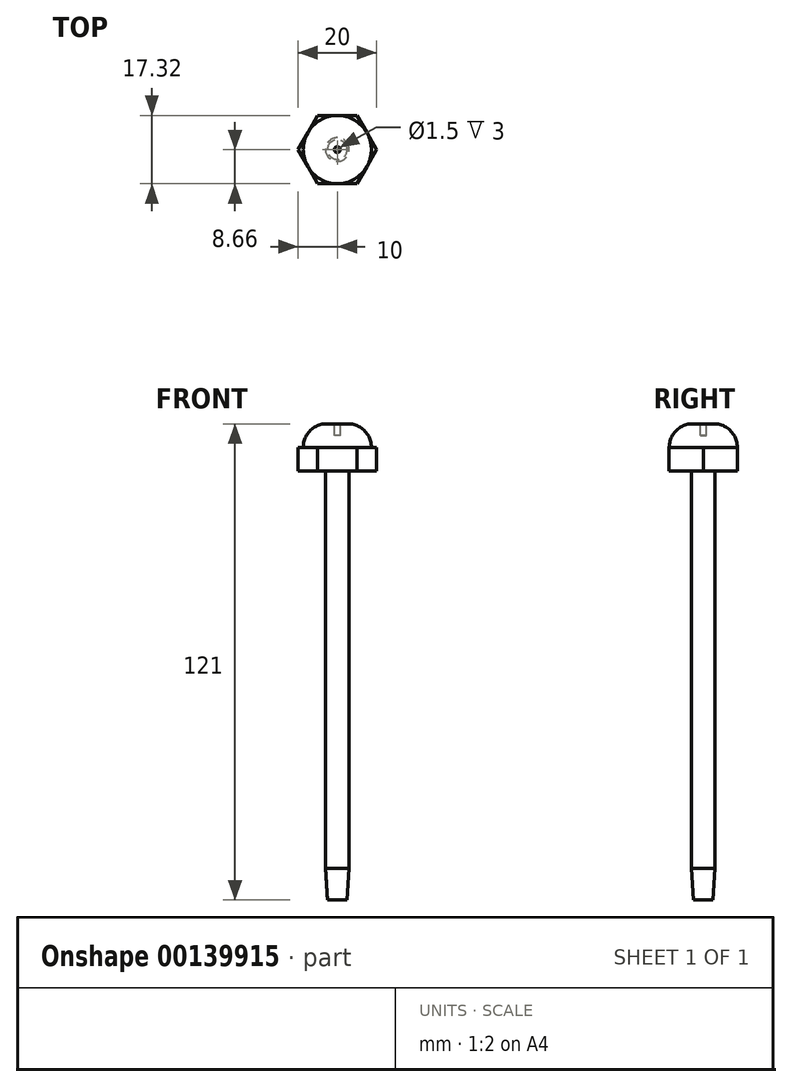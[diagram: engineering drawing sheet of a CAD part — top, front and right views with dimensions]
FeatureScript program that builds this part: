
annotation { "Feature Type Name" : "Feature", "Feature Type Description" : "" }
export const myFeature = defineFeature(function(context is Context, id is Id, definition is map)
    precondition{}
    {
        {
            var Q0;
            Q0=qCreatedBy(makeId("Top.planeOp"),FACE);
            var sketch = newSketch(context, id + "F0", { "sketchPlane" : qUnion([Q0])});
            skCircle(sketch, "E0", {"center": v(0, 0) * mm, "radius": 3 * mm});
            skLineSegment(sketch, "E1", {"start": v(-5, 8.66) * mm, "end": v(5, 8.66) * mm});
            skLineSegment(sketch, "E2", {"start": v(5, 8.66) * mm, "end": v(10, 0) * mm});
            skLineSegment(sketch, "E3", {"start": v(10, 0) * mm, "end": v(5, -8.66) * mm});
            skLineSegment(sketch, "E4", {"start": v(5, -8.66) * mm, "end": v(-5, -8.66) * mm});
            skLineSegment(sketch, "E5", {"start": v(-5, -8.66) * mm, "end": v(-10, 0) * mm});
            skLineSegment(sketch, "E6", {"start": v(-5, 8.66) * mm, "end": v(-10, 0) * mm});
            skLineSegment(sketch, "E7", {"start": v(-5, 8.66) * mm, "end": v(5, -8.66) * mm, "construction": true});
            skSolve(sketch);
        }
        {
            var Q0;
            Q0 = qSketchRegion(id + "F0", true);
            var Q1;
            Q1=makeQuery(id+"F0.imprint","IMPRINT",FACE,{"disambiguationData":[TD([[makeQuery(id+"F0.imprint","IMPRINT",EDGE,{"derivedFrom":sQuery(id+"F0.wireOp",EDGE,"E0")}),1.0]])]});
            extrude(context, id + "F1", {"entities" : qUnion([Q0, Q1]), "depth" : 6 * mm});
        }
        {
            var Q0;
            Q0=makeQuery(id+"F1.opExtrude","CAP_FACE",FACE,{"disambiguationData":[OSD([sQuery(id+"F0.wireOp",EDGE,"E1"),sQuery(id+"F0.wireOp",EDGE,"E2"),sQuery(id+"F0.wireOp",EDGE,"E3"),sQuery(id+"F0.wireOp",EDGE,"E4"),sQuery(id+"F0.wireOp",EDGE,"E5"),sQuery(id+"F0.wireOp",EDGE,"E6")])],"isStart":false});
            var sketch = newSketch(context, id + "F2", { "sketchPlane" : qUnion([Q0])});
            skCircle(sketch, "E8", {"center": v(0, 0) * mm, "radius": 8.66 * mm});
            skSolve(sketch);
        }
        {
            var Q0;
            Q0 = qSketchRegion(id + "F2", true);
            extrude(context, id + "F3", {"entities" : qUnion([Q0]), "operationType" : NewBodyOperationType.ADD, "depth" : 6 * mm});
        }
        {
            var Q0;
            Q0=makeQuery(id+"F3.opExtrude","CAP_EDGE",EDGE,{"disambiguationData":[OSD([sQuery(id+"F2.wireOp",EDGE,"E8")])],"isStart":false});
            fillet(context, id + "F4", {"entities" : qUnion([Q0]), "radius" : 6 * mm, "tangentPropagation" : true, "allowEdgeOverflow" : false});
        }
        {
            var Q0;
            Q0=makeQuery(id+"F3.opExtrude","CAP_FACE",FACE,{"disambiguationData":[OSD([sQuery(id+"F2.wireOp",EDGE,"E8")])],"isStart":false});
            var sketch = newSketch(context, id + "F5", { "sketchPlane" : qUnion([Q0])});
            skCircle(sketch, "E9", {"center": v(0, 0) * mm, "radius": 0.75 * mm});
            skSolve(sketch);
        }
        {
            var Q0;
            Q0 = qSketchRegion(id + "F5", true);
            extrude(context, id + "F6", {"entities" : qUnion([Q0]), "operationType" : NewBodyOperationType.REMOVE, "oppositeDirection" : true, "depth" : 3 * mm});
        }
        {
            var Q0;
            Q0=makeQuery(id+"F1.opExtrude","CAP_FACE",FACE,{"disambiguationData":[OSD([sQuery(id+"F0.wireOp",EDGE,"E1"),sQuery(id+"F0.wireOp",EDGE,"E2"),sQuery(id+"F0.wireOp",EDGE,"E3"),sQuery(id+"F0.wireOp",EDGE,"E4"),sQuery(id+"F0.wireOp",EDGE,"E5"),sQuery(id+"F0.wireOp",EDGE,"E6")])],"isStart":true});
            var sketch = newSketch(context, id + "F7", { "sketchPlane" : qUnion([Q0])});
            skCircle(sketch, "E10", {"center": v(0, 0) * mm, "radius": 3 * mm});
            skSolve(sketch);
        }
        {
            var Q0;
            Q0=makeQuery(id+"F7.imprint","IMPRINT",FACE,{"disambiguationData":[TD([[makeQuery(id+"F7.imprint","IMPRINT",EDGE,{"derivedFrom":sQuery(id+"F7.wireOp",EDGE,"E10")}),1.0]])]});
            extrude(context, id + "F8", {"entities" : qUnion([Q0]), "operationType" : NewBodyOperationType.ADD, "depth" : 101 * mm});
        }
        {
            var Q0;
            Q0=makeQuery(id+"F8.opExtrude","CAP_FACE",FACE,{"disambiguationData":[OSD([sQuery(id+"F7.wireOp",EDGE,"E10")])],"isStart":false});
            cPlane(context, id + "F9", {"entities" : qUnion([Q0]), "cplaneType" : CPlaneType.OFFSET, "offset" : 8 * mm, "width" : 150 * mm, "height" : 150 * mm});
        }
        {
            var Q0;
            Q0=qCreatedBy(id+"F9.planeOp",FACE);
            var sketch = newSketch(context, id + "F10", { "sketchPlane" : qUnion([Q0])});
            skCircle(sketch, "E11", {"center": v(0, 0) * mm, "radius": 2.5 * mm});
            skSolve(sketch);
        }
        {
            var Q0;
            Q0=makeQuery(id+"F8.opExtrude","CAP_FACE",FACE,{"disambiguationData":[OSD([sQuery(id+"F7.wireOp",EDGE,"E10")])],"isStart":false});
            var sketch = newSketch(context, id + "F11", { "sketchPlane" : qUnion([Q0])});
            skCircle(sketch, "E12", {"center": v(0, 0) * mm, "radius": 3 * mm});
            skSolve(sketch);
        }
        {
            var Q1;
            Q1 = qSketchRegion(id + "F10", true);
            var Q2;
            Q2 = qSketchRegion(id + "F11", true);
            loft(context, id + "F12", {"operationType" : NewBodyOperationType.ADD, "sheetProfilesArray" : [{ "sheetProfileEntities" : qUnion([Q1]) }, { "sheetProfileEntities" : qUnion([Q2]) }]});
        }
    });
